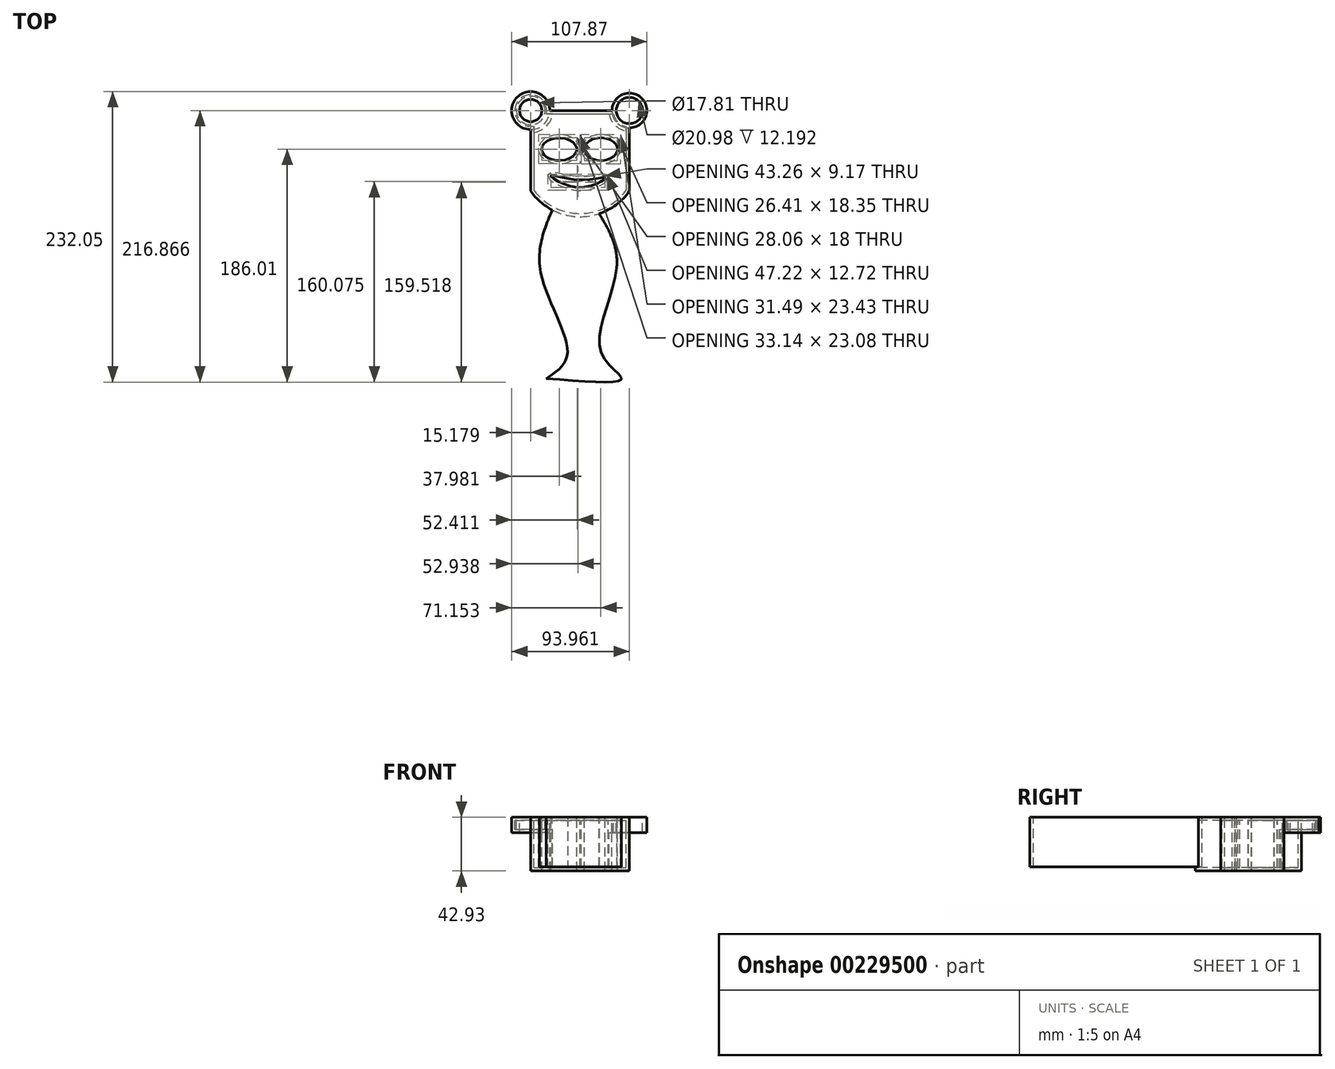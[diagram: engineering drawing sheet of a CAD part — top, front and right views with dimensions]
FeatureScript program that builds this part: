
annotation { "Feature Type Name" : "Feature", "Feature Type Description" : "" }
export const myFeature = defineFeature(function(context is Context, id is Id, definition is map)
    precondition{}
    {
        {
            var Q0;
            Q0=qCreatedBy(makeId("Top.planeOp"),FACE);
            var sketch = newSketch(context, id + "F0", { "sketchPlane" : qUnion([Q0])});
            skLineSegment(sketch, "E0.bottom", {"start": v(-24.2, 30.86) * mm, "end": v(25.48, 30.86) * mm});
            skLineSegment(sketch, "E0.top", {"start": v(-39.4, -33.53) * mm, "end": v(-20.92, -33.53) * mm});
            skLineSegment(sketch, "E0.left", {"start": v(-39.4, 15.67) * mm, "end": v(-39.4, -33.53) * mm});
            skLineSegment(sketch, "E0.right", {"start": v(39.4, 16.94) * mm, "end": v(39.4, -33.53) * mm});
            skCircle(sketch, "E1", {"center": v(-39.4, 30.86) * mm, "radius": 15.18 * mm});
            skCircle(sketch, "E2", {"center": v(39.4, 30.86) * mm, "radius": 13.91 * mm});
            skEllipse(sketch, "E3", {"center": v(-16.59, 0) * mm, "majorRadius": 14.03 * mm, "minorRadius": 9 * mm, "majorAxis": v(-1, 0)});
            skArc(sketch, "E4", {"start": v(-39.4, -33.53) * mm, "mid": v(0, -53.92) * mm, "end": v(39.4, -33.53) * mm});
            skArc(sketch, "E5", {"start": v(-20.92, -33.53) * mm, "mid": v(-0.2, -51.46) * mm, "end": v(20.5, -33.53) * mm});
            skEllipse(sketch, "E6", {"center": v(16.58, 0) * mm, "majorRadius": 13.2 * mm, "minorRadius": 9.17 * mm, "majorAxis": v(-1, 0)});
            skLineSegment(sketch, "E7.trimOffspring", {"start": v(20.5, -33.53) * mm, "end": v(39.4, -33.53) * mm});
            skCircle(sketch, "E8", {"center": v(39.4, 30.86) * mm, "radius": 10.5 * mm});
            skCircle(sketch, "E9", {"center": v(-39.4, 30.86) * mm, "radius": 8.9 * mm});
            skFitSpline(sketch, "E10", {"points": [v(20, -22.91) * mm, v(0, -24.57) * mm, v(-23.27, -21.2) * mm, v(-0.2, -30.53) * mm, v(20, -22.91) * mm]});
            skFitSpline(sketch, "E11", {"points": [v(-22.14, -48.54) * mm, v(-31.38, -98.44) * mm, v(-10.07, -162.94) * mm, v(-26.9, -183.13) * mm], "startDerivative": vector(-55.85, -132.84) * mm, "endDerivative": vector(-96.8, -63.08) * mm});
            skPoint(sketch, "E12.0.internal.snap0", {"position": v(-0.2, -51.46) * mm});
            skFitSpline(sketch, "E12", {"points": [v(15.19, -51.46) * mm, v(29.19, -95.07) * mm, v(16.85, -162.37) * mm, v(33.11, -183.13) * mm, v(-26.9, -183.13) * mm], "startDerivative": vector(97.4, -160.99) * mm, "endDerivative": vector(-322.25, 27.05) * mm});
            skFitSpline(sketch, "E13", {"points": [v(25.94, -71.95) * mm, v(66.73, -68.2) * mm, v(73.84, 5.6) * mm, v(93.53, -5.72) * mm, v(86.76, -82.9) * mm, v(29.19, -95.07) * mm], "startDerivative": vector(289.75, -73.56) * mm, "endDerivative": vector(-316.29, 20.96) * mm});
            skFitSpline(sketch, "E14", {"points": [v(-28.61, -63.93) * mm, v(-71.75, -54.2) * mm, v(-80.82, 6.52) * mm, v(-98.98, 22.8) * mm, v(-102.84, -54.57) * mm, v(-31.38, -98.44) * mm], "startDerivative": vector(-300.77, -10.04) * mm, "endDerivative": vector(363.15, -100.3) * mm});
            skSolve(sketch);
        }
        {
            var Q0;
            {var subQ2=sQuery(id+"F0.wireOp",EDGE,"E0.bottom");Q0=makeQuery(id+"F0.imprint","IMPRINT",FACE,{"disambiguationData":[TD([[makeQuery(id+"F0.imprint","IMPRINT",EDGE,{"derivedFrom":subQ2}),-1.0]])]});}
            extrude(context, id + "F1", {"entities" : qUnion([Q0]), "oppositeDirection" : true, "depth" : 42.93 * mm});
        }
        {
            var Q0;
            {var subQ0=sQuery(id+"F0.wireOp",EDGE,"E2");var subQ1=makeQuery(id+"F0.imprint","INTERSECT",VERTEX,{"derivedFrom":[sQuery(id+"F0.wireOp",EDGE,"E0.bottom"),subQ0]});Q0=makeQuery(id+"F0.imprint","IMPRINT",FACE,{"disambiguationData":[TD([[makeQuery(id+"F0.imprint","IMPRINT",EDGE,{"disambiguationData":[TD([[subQ1,-1.0]])],"derivedFrom":subQ0}),1.0]])]});}
            var Q1;
            {var subQ0=sQuery(id+"F0.wireOp",EDGE,"E1");var subQ1=makeQuery(id+"F0.imprint","INTERSECT",VERTEX,{"derivedFrom":[sQuery(id+"F0.wireOp",EDGE,"E0.bottom"),subQ0]});Q1=makeQuery(id+"F0.imprint","IMPRINT",FACE,{"disambiguationData":[TD([[makeQuery(id+"F0.imprint","IMPRINT",EDGE,{"disambiguationData":[TD([[subQ1,-1.0]])],"derivedFrom":subQ0}),1.0]])]});}
            extrude(context, id + "F2", {"entities" : qUnion([Q0, Q1]), "operationType" : NewBodyOperationType.ADD, "oppositeDirection" : true, "depth" : 12.2 * mm});
        }
        {
            var Q0;
            Q0=makeQuery(id+"F0.imprint","IMPRINT",FACE,{"disambiguationData":[TD([[makeQuery(id+"F0.imprint","IMPRINT",EDGE,{"derivedFrom":sQuery(id+"F0.wireOp",EDGE,"E0.top")}),-1.0]])]});
            extrude(context, id + "F3", {"entities" : qUnion([Q0]), "operationType" : NewBodyOperationType.ADD, "oppositeDirection" : true, "depth" : 42.93 * mm});
        }
        {
            var Q0;
            Q0=makeQuery(id+"F2.opExtrude","CAP_FACE",FACE,{"disambiguationData":[OSD([sQuery(id+"F0.wireOp",EDGE,"E2")])],"isStart":false});
            shell(context, id + "F4", {"entities" : qUnion([Q0]), "thickness" : 2.54 * mm});
        }
        {
            var Q0;
            {var subQ0=sQuery(id+"F0.wireOp",EDGE,"E11");Q0=makeQuery(id+"F0.imprint","IMPRINT",FACE,{"disambiguationData":[TD([[makeQuery(id+"F0.imprint","IMPRINT",EDGE,{"derivedFrom":subQ0}),1.0]])]});}
            extrude(context, id + "F5", {"entities" : qUnion([Q0]), "operationType" : NewBodyOperationType.ADD, "oppositeDirection" : true, "depth" : 39.62 * mm});
        }
    });
